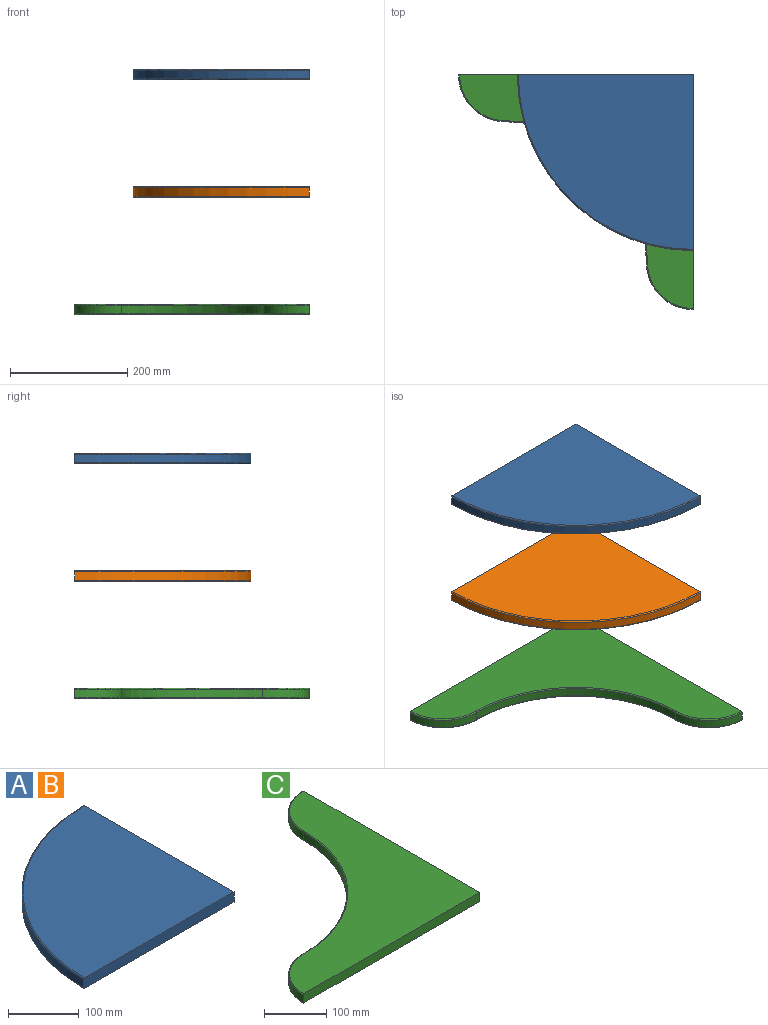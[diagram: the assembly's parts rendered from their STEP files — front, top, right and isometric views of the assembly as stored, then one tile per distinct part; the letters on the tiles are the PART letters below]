
ASSEMBLY  parts=3 mates=6
PART A: 7 faces, bbox 324.7x324.7x18 mm
  f0: cylinder r=300mm len=300mm, axis (0,0,-1), area 6785.8mm2, adj f1,f2,f5,f6
  f1: plane 300x18mm, normal (0,-1,0), area 5398.6mm2, adj f0,f2,f3,f4,f5,f6
  f2: plane 300x18mm, normal (1,0,0), area 5398.6mm2, adj f0,f1,f3,f4,f5,f6
  f3: plane 298.2x298.2mm, normal (0,0,1), area 69840.1mm2, adj f1,f2,f6
  f4: plane 298.2x298.2mm, normal (0,0,-1), area 69840.1mm2, adj f1,f2,f5
  f5: torus R=298.2mm, axis (0,0,1), area 1329.5mm2, adj f0,f1,f2,f4
  f6: torus R=298.2mm, axis (0,0,1), area 1329.5mm2, adj f0,f1,f2,f3
PART B: same geometry as A
PART C: 13 faces, bbox 406.6x406.6x18 mm
  f0: plane 400x18mm, normal (0,-1,0), area 7198.6mm2, adj f1,f4,f5,f6,f7,f10
  f1: plane 400x18mm, normal (1,0,0), area 7198.6mm2, adj f0,f2,f5,f6,f8,f11
  f2: cylinder r=80mm len=80mm, axis (0,0,-1), area 1809.6mm2, adj f1,f3,f8,f11
  f3: cylinder r=240mm len=240mm, axis (0,0,-1), area 5428.7mm2, adj f2,f4,f9,f12
  f4: cylinder r=80mm len=80mm, axis (0,0,-1), area 1809.6mm2, adj f0,f3,f7,f10
  f5: plane 398.2x398.2mm, normal (0,0,1), area 66085.7mm2, adj f0,f1,f10,f11,f12
  f6: plane 398.2x398.2mm, normal (0,0,-1), area 66085.7mm2, adj f0,f1,f7,f8,f9
  f7: torus R=78.2mm, axis (0,0,1), area 352.4mm2, adj f0,f4,f6,f9
  f8: torus R=78.2mm, axis (0,0,1), area 352.4mm2, adj f1,f2,f6,f9
  f9: torus R=241.8mm, axis (0,0,1), area 1068.8mm2, adj f3,f6,f7,f8
  f10: torus R=78.2mm, axis (0,0,1), area 352.4mm2, adj f0,f4,f5,f12
  f11: torus R=78.2mm, axis (0,0,1), area 352.4mm2, adj f1,f2,f5,f12
  f12: torus R=241.8mm, axis (0,0,1), area 1068.8mm2, adj f3,f5,f10,f11
PLACE A rot(axis=(0,0,1),90deg) t=(-259.32,228.04,-132.92)mm
PLACE B rot(axis=(0,0,1),90deg) t=(-259.32,228.04,-332.92)mm
PLACE C rot(axis=(0,0,1),90deg) t=(-259.32,228.04,-532.92)mm
MATE planar C.f1 <-> A.f2  axis (0,1,0) through (-459.28,228.04,-523.92)mm
MATE planar B.f1 <-> C.f0  axis (1,0,0) through (-259.32,78.07,-323.92)mm
MATE planar B.f2 <-> A.f2  axis (0,1,0) through (-409.28,228.04,-323.92)mm
MATE parallel B.f3 <-> A.f3  axis (0,0,1) through (-385.88,101.48,-314.92)mm
MATE parallel B.f3 <-> C.f5  axis (0,0,1) through (-385.88,101.48,-314.92)mm
MATE planar A.f1 <-> B.f1  axis (1,0,0) through (-259.32,78.07,-123.92)mm
